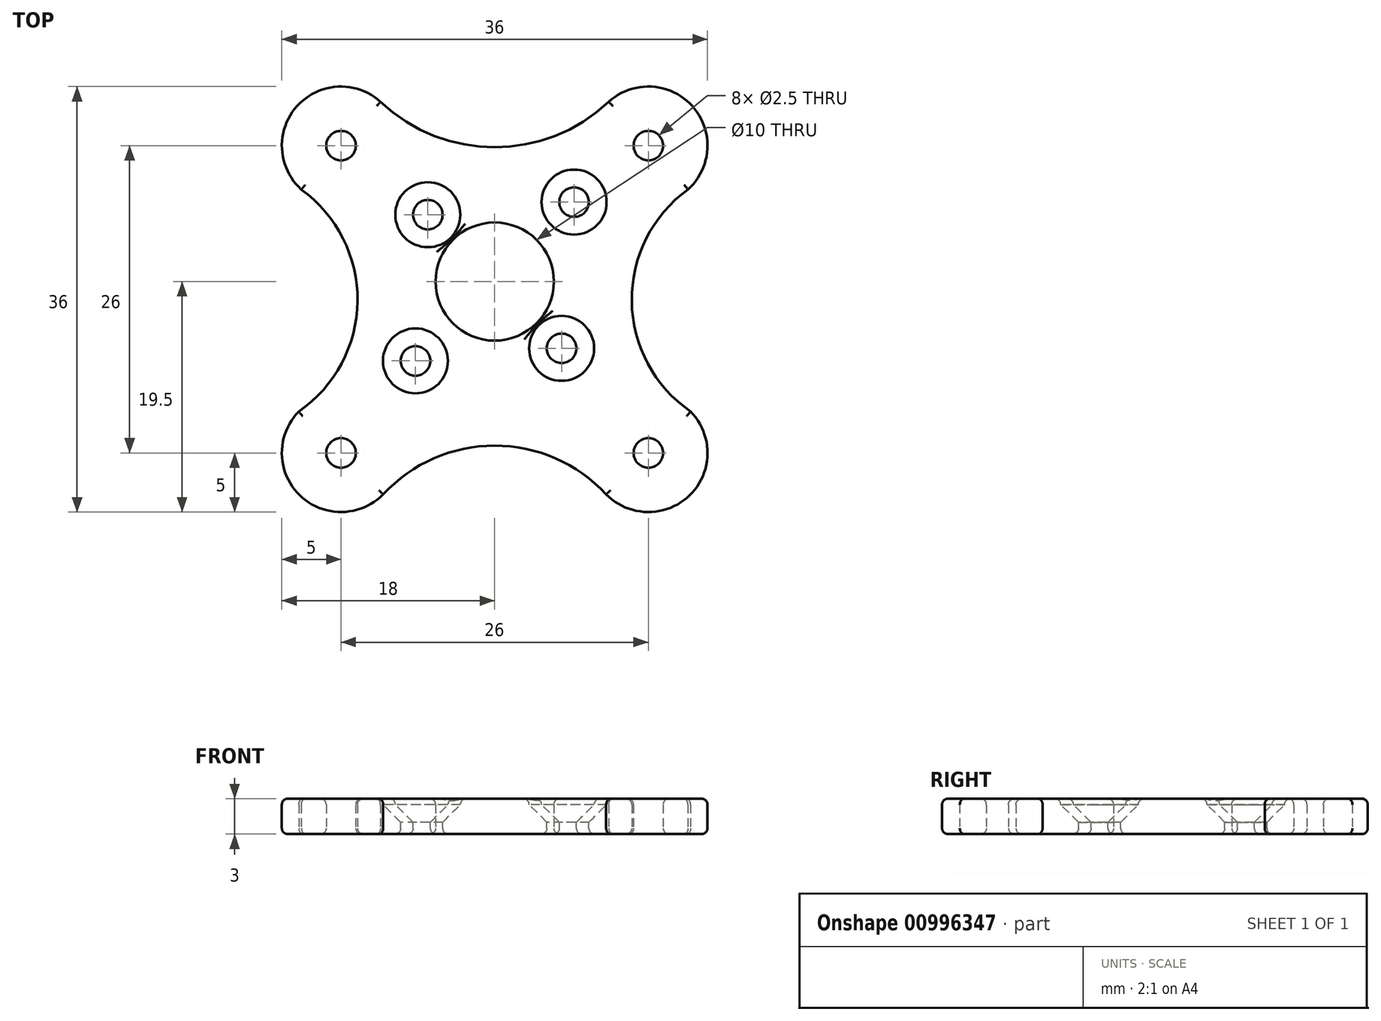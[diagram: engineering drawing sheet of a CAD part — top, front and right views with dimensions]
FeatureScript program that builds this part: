
annotation { "Feature Type Name" : "Feature", "Feature Type Description" : "" }
export const myFeature = defineFeature(function(context is Context, id is Id, definition is map)
    precondition{}
    {
        {
            var Q0;
            Q0=qCreatedBy(makeId("Top.planeOp"),FACE);
            var sketch = newSketch(context, id + "F0", { "sketchPlane" : qUnion([Q0])});
            skCircle(sketch, "E0", {"center": v(0, 0) * mm, "radius": 1.25 * mm});
            skCircle(sketch, "E1", {"center": v(0, 0) * mm, "radius": 5 * mm});
            skCircle(sketch, "E2.0.1.0", {"center": v(0, 26) * mm, "radius": 5 * mm});
            skCircle(sketch, "E2.0.1.1", {"center": v(0, 26) * mm, "radius": 1.25 * mm});
            skCircle(sketch, "E2.1.0.0", {"center": v(26, 0) * mm, "radius": 5 * mm});
            skCircle(sketch, "E2.1.0.1", {"center": v(26, 0) * mm, "radius": 1.25 * mm});
            skCircle(sketch, "E2.1.1.0", {"center": v(26, 26) * mm, "radius": 5 * mm});
            skCircle(sketch, "E2.1.1.1", {"center": v(26, 26) * mm, "radius": 1.25 * mm});
            skLineSegment(sketch, "E2.direction1", {"start": v(0, 0) * mm, "end": v(26, 0) * mm, "construction": true});
            skLineSegment(sketch, "E2.direction2", {"start": v(0, 0) * mm, "end": v(0, 26) * mm, "construction": true});
            skLineSegment(sketch, "E3", {"start": v(13, 0) * mm, "end": v(13, 14.5) * mm});
            skCircle(sketch, "E4", {"center": v(13, 14.5) * mm, "radius": 5 * mm});
            skCircle(sketch, "E5", {"center": v(13, 14.5) * mm, "radius": 8 * mm});
            skCircle(sketch, "E6", {"center": v(13, 14.5) * mm, "radius": 9.5 * mm});
            skArc(sketch, "E7", {"start": v(3.35, 29.71) * mm, "mid": v(13, 25.87) * mm, "end": v(22.65, 29.71) * mm});
            skArc(sketch, "E8", {"start": v(22.43, -3.5) * mm, "mid": v(13, 0.62) * mm, "end": v(3.57, -3.5) * mm});
            skArc(sketch, "E9", {"start": v(-3.57, 3.5) * mm, "mid": v(1.4, 12.84) * mm, "end": v(-3.35, 22.29) * mm});
            skArc(sketch, "E10", {"start": v(29.35, 22.29) * mm, "mid": v(24.6, 12.84) * mm, "end": v(29.57, 3.5) * mm});
            skLineSegment(sketch, "E11", {"start": v(3.5, 5) * mm, "end": v(22.5, 24) * mm});
            skLineSegment(sketch, "E12", {"start": v(3.5, 24) * mm, "end": v(22.5, 5) * mm});
            skSolve(sketch);
        }
        {
            var Q0;
            {var subQ0=sQuery(id+"F0.wireOp",EDGE,"QqaoAoN3-Hv4W-iVoq-AS4z-YvYTliRH1W30");var subQ1=sQuery(id+"F0.wireOp",EDGE,"E5");var subQ2=makeQuery(id+"F0.imprint","INTERSECT",VERTEX,{"derivedFrom":[subQ1,subQ0]});Q0=makeQuery(id+"F0.imprint","IMPRINT",FACE,{"disambiguationData":[TD([[makeQuery(id+"F0.imprint","IMPRINT",EDGE,{"disambiguationData":[TD([[subQ2,-1.0]])],"derivedFrom":subQ1}),-1.0]])]});}
            var Q1;
            {var subQ0=sQuery(id+"F0.wireOp",EDGE,"34HKzcNe-Xheh-t07d-8Ypu-uIPqtfcBvWmb");var subQ1=sQuery(id+"F0.wireOp",EDGE,"E5");var subQ2=makeQuery(id+"F0.imprint","INTERSECT",VERTEX,{"disambiguationData":[OD(1.0)],"derivedFrom":[subQ1,subQ0]});Q1=makeQuery(id+"F0.imprint","IMPRINT",FACE,{"disambiguationData":[TD([[makeQuery(id+"F0.imprint","IMPRINT",EDGE,{"disambiguationData":[TD([[subQ2,-1.0]])],"derivedFrom":subQ1}),-1.0]])]});}
            var Q2;
            {var subQ1=sQuery(id+"F0.wireOp",EDGE,"E1");var subQ5=sQuery(id+"F0.wireOp",EDGE,"34HKzcNe-Xheh-t07d-8Ypu-uIPqtfcBvWmb");var subQ6=makeQuery(id+"F0.imprint","INTERSECT",VERTEX,{"derivedFrom":[subQ1,subQ5]});Q2=makeQuery(id+"F0.imprint","IMPRINT",FACE,{"disambiguationData":[TD([[makeQuery(id+"F0.imprint","IMPRINT",EDGE,{"disambiguationData":[TD([[subQ6,1.0]])],"derivedFrom":subQ1}),-1.0]])]});}
            var Q3;
            {var subQ0=sQuery(id+"F0.wireOp",EDGE,"E5");var subQ1=sQuery(id+"F0.wireOp",EDGE,"E3");var subQ2=makeQuery(id+"F0.imprint","INTERSECT",VERTEX,{"derivedFrom":[subQ1,subQ0]});Q3=makeQuery(id+"F0.imprint","IMPRINT",FACE,{"disambiguationData":[TD([[makeQuery(id+"F0.imprint","IMPRINT",EDGE,{"disambiguationData":[TD([[subQ2,1.0]])],"derivedFrom":subQ0}),-1.0]])]});}
            var Q4;
            {var subQ0=sQuery(id+"F0.wireOp",EDGE,"E5");var subQ1=sQuery(id+"F0.wireOp",EDGE,"E3");var subQ2=makeQuery(id+"F0.imprint","INTERSECT",VERTEX,{"derivedFrom":[subQ1,subQ0]});Q4=makeQuery(id+"F0.imprint","IMPRINT",FACE,{"disambiguationData":[TD([[makeQuery(id+"F0.imprint","IMPRINT",EDGE,{"disambiguationData":[TD([[subQ2,-1.0]])],"derivedFrom":subQ0}),-1.0]])]});}
            var Q5;
            {var subQ0=sQuery(id+"F0.wireOp",EDGE,"E5");var subQ1=sQuery(id+"F0.wireOp",EDGE,"E3");var subQ2=makeQuery(id+"F0.imprint","INTERSECT",VERTEX,{"derivedFrom":[subQ1,subQ0]});Q5=makeQuery(id+"F0.imprint","IMPRINT",FACE,{"disambiguationData":[TD([[makeQuery(id+"F0.imprint","IMPRINT",EDGE,{"disambiguationData":[TD([[subQ2,-1.0]])],"derivedFrom":subQ1}),-1.0]])]});}
            var Q6;
            {var subQ0=sQuery(id+"F0.wireOp",EDGE,"E5");var subQ1=sQuery(id+"F0.wireOp",EDGE,"E3");var subQ2=makeQuery(id+"F0.imprint","INTERSECT",VERTEX,{"derivedFrom":[subQ1,subQ0]});Q6=makeQuery(id+"F0.imprint","IMPRINT",FACE,{"disambiguationData":[TD([[makeQuery(id+"F0.imprint","IMPRINT",EDGE,{"disambiguationData":[TD([[subQ2,-1.0]])],"derivedFrom":subQ1}),1.0]])]});}
            var Q7;
            {var subQ0=sQuery(id+"F0.wireOp",EDGE,"34HKzcNe-Xheh-t07d-8Ypu-uIPqtfcBvWmb");var subQ1=sQuery(id+"F0.wireOp",EDGE,"E5");var subQ2=makeQuery(id+"F0.imprint","INTERSECT",VERTEX,{"disambiguationData":[OD(1.0)],"derivedFrom":[subQ1,subQ0]});Q7=makeQuery(id+"F0.imprint","IMPRINT",FACE,{"disambiguationData":[TD([[makeQuery(id+"F0.imprint","IMPRINT",EDGE,{"disambiguationData":[TD([[subQ2,-1.0]])],"derivedFrom":subQ1}),1.0]])]});}
            var Q8;
            {var subQ1=sQuery(id+"F0.wireOp",EDGE,"E2.0.1.0");var subQ7=sQuery(id+"F0.wireOp",EDGE,"NoI2qd9F-FtKE-tBs8-2il7-RFN8TzHUUGqv.left");var subQ8=makeQuery(id+"F0.imprint","INTERSECT",VERTEX,{"derivedFrom":[subQ1,subQ7]});Q8=makeQuery(id+"F0.imprint","IMPRINT",FACE,{"disambiguationData":[TD([[makeQuery(id+"F0.imprint","IMPRINT",EDGE,{"disambiguationData":[TD([[subQ8,-1.0]])],"derivedFrom":subQ1}),-1.0]])]});}
            var Q9;
            {var subQ0=sQuery(id+"F0.wireOp",EDGE,"34HKzcNe-Xheh-t07d-8Ypu-uIPqtfcBvWmb");var subQ1=sQuery(id+"F0.wireOp",EDGE,"E1");var subQ2=makeQuery(id+"F0.imprint","INTERSECT",VERTEX,{"derivedFrom":[subQ1,subQ0]});Q9=makeQuery(id+"F0.imprint","IMPRINT",FACE,{"disambiguationData":[TD([[makeQuery(id+"F0.imprint","IMPRINT",EDGE,{"disambiguationData":[TD([[subQ2,-1.0]])],"derivedFrom":subQ1}),-1.0]])]});}
            var Q10;
            Q10=makeQuery(id+"F0.imprint","IMPRINT",FACE,{"disambiguationData":[TD([[makeQuery(id+"F0.imprint","IMPRINT",EDGE,{"derivedFrom":sQuery(id+"F0.wireOp",EDGE,"E2.0.1.1")}),-1.0]])]});
            var Q11;
            Q11=makeQuery(id+"F0.imprint","IMPRINT",FACE,{"disambiguationData":[TD([[makeQuery(id+"F0.imprint","IMPRINT",EDGE,{"derivedFrom":sQuery(id+"F0.wireOp",EDGE,"E2.1.1.1")}),-1.0]])]});
            var Q12;
            Q12=makeQuery(id+"F0.imprint","IMPRINT",FACE,{"disambiguationData":[TD([[makeQuery(id+"F0.imprint","IMPRINT",EDGE,{"derivedFrom":sQuery(id+"F0.wireOp",EDGE,"E2.1.0.1")}),-1.0]])]});
            var Q13;
            Q13=makeQuery(id+"F0.imprint","IMPRINT",FACE,{"disambiguationData":[TD([[makeQuery(id+"F0.imprint","IMPRINT",EDGE,{"derivedFrom":sQuery(id+"F0.wireOp",EDGE,"E0")}),-1.0]])]});
            var Q14;
            {var subQ0=sQuery(id+"F0.wireOp",EDGE,"E12");var subQ1=sQuery(id+"F0.wireOp",EDGE,"E4");var subQ2=makeQuery(id+"F0.imprint","INTERSECT",VERTEX,{"disambiguationData":[OD(0.0)],"derivedFrom":[subQ1,subQ0]});Q14=makeQuery(id+"F0.imprint","IMPRINT",FACE,{"disambiguationData":[TD([[makeQuery(id+"F0.imprint","IMPRINT",EDGE,{"disambiguationData":[TD([[subQ2,-1.0]])],"derivedFrom":subQ1}),-1.0]])]});}
            var Q15;
            {var subQ0=sQuery(id+"F0.wireOp",EDGE,"E12");var subQ1=sQuery(id+"F0.wireOp",EDGE,"E4");var subQ2=makeQuery(id+"F0.imprint","INTERSECT",VERTEX,{"disambiguationData":[OD(0.0)],"derivedFrom":[subQ1,subQ0]});Q15=makeQuery(id+"F0.imprint","IMPRINT",FACE,{"disambiguationData":[TD([[makeQuery(id+"F0.imprint","IMPRINT",EDGE,{"disambiguationData":[TD([[subQ2,1.0]])],"derivedFrom":subQ1}),-1.0]])]});}
            var Q16;
            {var subQ0=sQuery(id+"F0.wireOp",EDGE,"E11");var subQ1=sQuery(id+"F0.wireOp",EDGE,"E4");var subQ2=makeQuery(id+"F0.imprint","INTERSECT",VERTEX,{"disambiguationData":[OD(0.0)],"derivedFrom":[subQ1,subQ0]});Q16=makeQuery(id+"F0.imprint","IMPRINT",FACE,{"disambiguationData":[TD([[makeQuery(id+"F0.imprint","IMPRINT",EDGE,{"disambiguationData":[TD([[subQ2,1.0]])],"derivedFrom":subQ1}),-1.0]])]});}
            var Q17;
            {var subQ7=sQuery(id+"F0.wireOp",EDGE,"E10");var subQ12=sQuery(id+"F0.wireOp",EDGE,"E2.1.0.0");var subQ13=makeQuery(id+"F0.imprint","INTERSECT",VERTEX,{"disambiguationData":[OD(1.0)],"derivedFrom":[subQ12,subQ7]});Q17=makeQuery(id+"F0.imprint","IMPRINT",FACE,{"disambiguationData":[TD([[makeQuery(id+"F0.imprint","IMPRINT",EDGE,{"disambiguationData":[TD([[subQ13,-1.0]])],"derivedFrom":subQ12}),-1.0]])]});}
            extrude(context, id + "F1", {"entities" : qUnion([Q0, Q1, Q2, Q3, Q4, Q5, Q6, Q7, Q8, Q9, Q10, Q11, Q12, Q13, Q14, Q15, Q16, Q17]), "depth" : 2.5 * mm, "offsetDistance" : 25 * mm});
        }
        {
            var Q0;
            Q0=makeQuery(id+"F1.opExtrude","CAP_FACE",FACE,{"disambiguationData":[OSD([sQuery(id+"F0.wireOp",EDGE,"E0"),sQuery(id+"F0.wireOp",EDGE,"E1"),sQuery(id+"F0.wireOp",EDGE,"E2.0.1.0"),sQuery(id+"F0.wireOp",EDGE,"E2.0.1.1"),sQuery(id+"F0.wireOp",EDGE,"E2.1.0.0"),sQuery(id+"F0.wireOp",EDGE,"E2.1.0.1"),sQuery(id+"F0.wireOp",EDGE,"E2.1.1.0"),sQuery(id+"F0.wireOp",EDGE,"E2.1.1.1"),sQuery(id+"F0.wireOp",EDGE,"E4"),sQuery(id+"F0.wireOp",EDGE,"E7"),sQuery(id+"F0.wireOp",EDGE,"E8"),sQuery(id+"F0.wireOp",EDGE,"E9"),sQuery(id+"F0.wireOp",EDGE,"E10")])],"isStart":false});
            var sketch = newSketch(context, id + "F2", { "sketchPlane" : qUnion([Q0])});
            skCircle(sketch, "E13", {"center": v(6.3, 7.79) * mm, "radius": 0.22 * mm});
            skCircle(sketch, "E14", {"center": v(19.71, 21.22) * mm, "radius": 0.09 * mm});
            skCircle(sketch, "E15", {"center": v(7.35, 20.16) * mm, "radius": 0.06 * mm});
            skCircle(sketch, "E16", {"center": v(18.66, 8.85) * mm, "radius": 0.1 * mm});
            skSolve(sketch);
        }
        {
            var Q0;
            Q0=sQuery(id+"F2.wireOp",VERTEX,"E13.center");
            var Q1;
            Q1=sQuery(id+"F2.wireOp",VERTEX,"E16.center");
            var Q2;
            Q2=sQuery(id+"F2.wireOp",VERTEX,"E15.center");
            var Q3;
            Q3=sQuery(id+"F2.wireOp",VERTEX,"E14.center");
            var Q4;
            Q4=makeQuery(id+"F1.opExtrude","SWEPT_BODY",BODY,{"disambiguationData":[OSD([sQuery(id+"F0.wireOp",EDGE,"E0"),sQuery(id+"F0.wireOp",EDGE,"E1"),sQuery(id+"F0.wireOp",EDGE,"E2.0.1.0"),sQuery(id+"F0.wireOp",EDGE,"E2.0.1.1"),sQuery(id+"F0.wireOp",EDGE,"E2.1.0.0"),sQuery(id+"F0.wireOp",EDGE,"E2.1.0.1"),sQuery(id+"F0.wireOp",EDGE,"E2.1.1.0"),sQuery(id+"F0.wireOp",EDGE,"E2.1.1.1"),sQuery(id+"F0.wireOp",EDGE,"E4"),sQuery(id+"F0.wireOp",EDGE,"E7"),sQuery(id+"F0.wireOp",EDGE,"E8"),sQuery(id+"F0.wireOp",EDGE,"E9"),sQuery(id+"F0.wireOp",EDGE,"E10")])]});
            hole(context, id + "F3", {"style" : HoleStyle.C_SINK, "endStyle" : HoleEndStyle.THROUGH, "holeDiameter" : 2.5 * mm, "cSinkDiameter" : 5.5 * mm, "cSinkAngle" : 90 * degree, "majorDiameter" : 5 * mm, "isTappedThrough" : true, "tappedDepth" : 12 * mm, "tapClearance" : 3, "startFromSketch" : true, "locations" : qUnion([Q0, Q1, Q2, Q3]), "scope" : qUnion([Q4])});
        }
        {
            var Q0;
            Q0=makeQuery(id+"F1.opExtrude","CAP_FACE",FACE,{"disambiguationData":[OSD([sQuery(id+"F0.wireOp",EDGE,"E0"),sQuery(id+"F0.wireOp",EDGE,"E1"),sQuery(id+"F0.wireOp",EDGE,"E2.0.1.0"),sQuery(id+"F0.wireOp",EDGE,"E2.0.1.1"),sQuery(id+"F0.wireOp",EDGE,"E2.1.0.0"),sQuery(id+"F0.wireOp",EDGE,"E2.1.0.1"),sQuery(id+"F0.wireOp",EDGE,"E2.1.1.0"),sQuery(id+"F0.wireOp",EDGE,"E2.1.1.1"),sQuery(id+"F0.wireOp",EDGE,"E4"),sQuery(id+"F0.wireOp",EDGE,"E7"),sQuery(id+"F0.wireOp",EDGE,"E8"),sQuery(id+"F0.wireOp",EDGE,"E9"),sQuery(id+"F0.wireOp",EDGE,"E10")])],"isStart":false});
            extrude(context, id + "F4", {"entities" : qUnion([Q0]), "operationType" : NewBodyOperationType.ADD, "depth" : 0.5 * mm, "offsetDistance" : 25 * mm});
        }
        {
            var Q0;
            Q0=makeQuery(id+"F4.opExtrude","CAP_FACE",FACE,{"disambiguationData":[OSD([sQuery(id+"F0.wireOp",EDGE,"E0"),sQuery(id+"F0.wireOp",EDGE,"E1"),sQuery(id+"F0.wireOp",EDGE,"E2.0.1.0"),sQuery(id+"F0.wireOp",EDGE,"E2.0.1.1"),sQuery(id+"F0.wireOp",EDGE,"E2.1.0.0"),sQuery(id+"F0.wireOp",EDGE,"E2.1.0.1"),sQuery(id+"F0.wireOp",EDGE,"E2.1.1.0"),sQuery(id+"F0.wireOp",EDGE,"E2.1.1.1"),sQuery(id+"F0.wireOp",EDGE,"E4"),sQuery(id+"F0.wireOp",EDGE,"E7"),sQuery(id+"F0.wireOp",EDGE,"E8"),sQuery(id+"F0.wireOp",EDGE,"E9"),sQuery(id+"F0.wireOp",EDGE,"E10")])],"isStart":false});
            fillet(context, id + "F5", {"entities" : qUnion([Q0]), "radius" : 0.5 * mm, "tangentPropagation" : true, "allowEdgeOverflow" : false});
        }
        {
            var Q0;
            Q0=makeQuery(id+"F1.opExtrude","CAP_FACE",FACE,{"disambiguationData":[OSD([sQuery(id+"F0.wireOp",EDGE,"E0"),sQuery(id+"F0.wireOp",EDGE,"E1"),sQuery(id+"F0.wireOp",EDGE,"E2.0.1.0"),sQuery(id+"F0.wireOp",EDGE,"E2.0.1.1"),sQuery(id+"F0.wireOp",EDGE,"E2.1.0.0"),sQuery(id+"F0.wireOp",EDGE,"E2.1.0.1"),sQuery(id+"F0.wireOp",EDGE,"E2.1.1.0"),sQuery(id+"F0.wireOp",EDGE,"E2.1.1.1"),sQuery(id+"F0.wireOp",EDGE,"E4"),sQuery(id+"F0.wireOp",EDGE,"E7"),sQuery(id+"F0.wireOp",EDGE,"E8"),sQuery(id+"F0.wireOp",EDGE,"E9"),sQuery(id+"F0.wireOp",EDGE,"E10")])],"isStart":true});
            fillet(context, id + "F6", {"entities" : qUnion([Q0]), "radius" : 0.5 * mm, "tangentPropagation" : true, "allowEdgeOverflow" : false});
        }
    });
